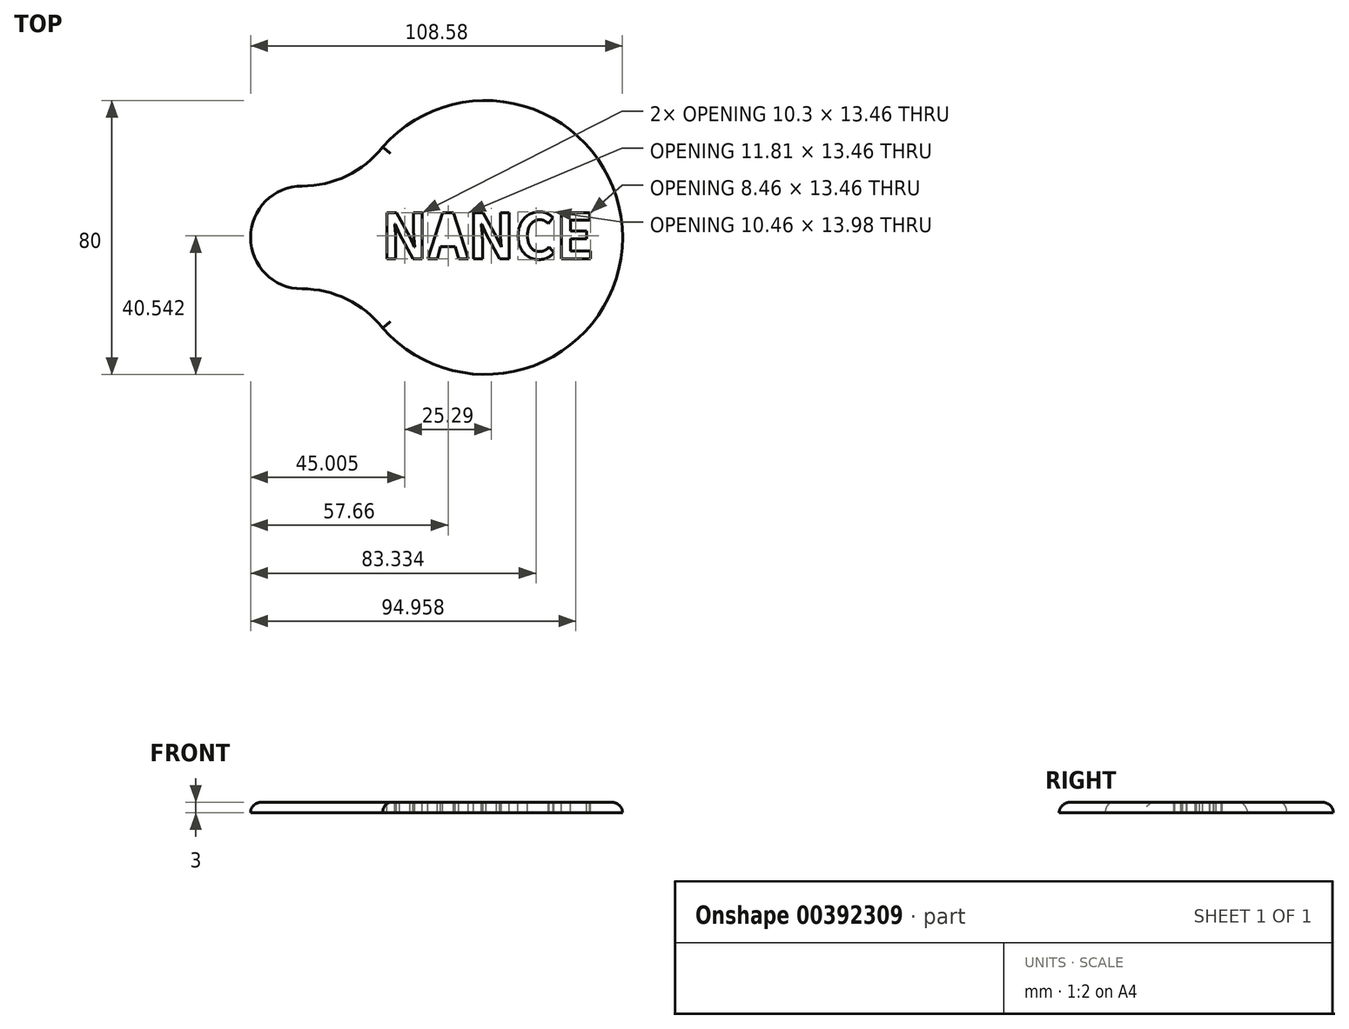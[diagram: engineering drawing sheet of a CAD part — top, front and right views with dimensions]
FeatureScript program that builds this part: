
annotation { "Feature Type Name" : "Feature", "Feature Type Description" : "" }
export const myFeature = defineFeature(function(context is Context, id is Id, definition is map)
    precondition{}
    {
        {
            var Q0;
            Q0=qCreatedBy(makeId("Top.planeOp"),FACE);
            var sketch = newSketch(context, id + "F0", { "sketchPlane" : qUnion([Q0])});
            skLineSegment(sketch, "E0.left", {"start": v(30, 0) * mm, "end": v(30, 0) * mm});
            skLineSegment(sketch, "E0.right", {"start": v(-30, -10) * mm, "end": v(-30, -10) * mm});
            skPoint(sketch, "E0.middle", {"position": v(0, 0) * mm});
            skPoint(sketch, "E1.visualSharp", {"position": v(30, 40) * mm});
            skPoint(sketch, "E2.visualSharp", {"position": v(30, -40) * mm});
            skPoint(sketch, "E3.visualSharp", {"position": v(-30, -40) * mm});
            skLineSegment(sketch, "E4.bottom", {"start": v(-45, 15) * mm, "end": v(-45, 15) * mm});
            skLineSegment(sketch, "E4.top", {"start": v(-45, -15) * mm, "end": v(-45, -15) * mm});
            skPoint(sketch, "E4.middle", {"position": v(-37.5, 0) * mm});
            skArc(sketch, "E5", {"start": v(-45, -15) * mm, "mid": v(-60, 0) * mm, "end": v(-45, 15) * mm});
            skPoint(sketch, "E6.visualSharp", {"position": v(-30, 40) * mm});
            skPoint(sketch, "E7.newPointA", {"position": v(-30, 15) * mm});
            skArc(sketch, "E7.filletArc", {"start": v(-45, 15) * mm, "mid": v(-31.9, 18.01) * mm, "end": v(-21.43, 26.44) * mm});
            skPoint(sketch, "E8.newPointA", {"position": v(-30, -15) * mm});
            skArc(sketch, "E8.filletArc", {"start": v(-21.43, -26.44) * mm, "mid": v(-31.9, -18.01) * mm, "end": v(-45, -15) * mm});
            skArc(sketch, "E9", {"start": v(-21.43, -26.44) * mm, "mid": v(48.58, 0) * mm, "end": v(-21.43, 26.44) * mm});
            skSolve(sketch);
        }
        {
            var Q0;
            Q0=qSketchRegion(id+"F0",true);
            extrude(context, id + "F1", {"entities" : qUnion([Q0]), "depth" : 3 * mm});
        }
        {
            var Q0;
            Q0=makeQuery(id+"F1.opExtrude","CAP_EDGE",EDGE,{"disambiguationData":[OSD([sQuery(id+"F0.wireOp",EDGE,"E9")])],"isStart":false});
            var Q1;
            Q1=makeQuery(id+"F1.opExtrude","CAP_EDGE",EDGE,{"disambiguationData":[OSD([sQuery(id+"F0.wireOp",EDGE,"E7.filletArc")])],"isStart":false});
            var Q2;
            Q2=makeQuery(id+"F1.opExtrude","CAP_EDGE",EDGE,{"disambiguationData":[OSD([sQuery(id+"F0.wireOp",EDGE,"E5")])],"isStart":false});
            fillet(context, id + "F2", {"entities" : qUnion([Q0, Q1, Q2]), "radius" : 3 * mm, "tangentPropagation" : true, "allowEdgeOverflow" : false});
        }
        {
            var Q0;
            Q0=makeQuery(id+"F1.opExtrude","CAP_FACE",FACE,{"disambiguationData":[OSD([sQuery(id+"F0.wireOp",EDGE,"E5"),sQuery(id+"F0.wireOp",EDGE,"E7.filletArc"),sQuery(id+"F0.wireOp",EDGE,"E8.filletArc"),sQuery(id+"F0.wireOp",EDGE,"E9")])],"isStart":false});
            var sketch = newSketch(context, id + "F3", { "sketchPlane" : qUnion([Q0])});
            skText(sketch, "E10", { "text": "NANCE\n", "fontName": "NotoSansCJKsc-Bold.otf"});
            const initialGuessF3  = {"E10": [-0.0218, -0.00619, 1, 0, 0.0131]};
            skSetInitialGuess(sketch, initialGuessF3);
            skSolve(sketch);
        }
        {
            var Q0;
            Q0 = qSketchRegion(id + "F3", true);
            extrude(context, id + "F4", {"entities" : qUnion([Q0]), "operationType" : NewBodyOperationType.REMOVE, "oppositeDirection" : true, "depth" : 25 * mm});
        }
        {
            var Q0;
            Q0=makeQuery(id+"F4.boolean.opBoolean","SPLIT",FACE,{"disambiguationData":[TD([makeQuery(id+"F4.opExtrude","SWEPT_FACE",FACE,{"disambiguationData":[OSD([sQuery(id+"F3.wireOp",EDGE,"E10.sketch_text.stroke-16")])]})])],"derivedFrom":makeQuery(id+"F1.opExtrude","CAP_FACE",FACE,{"disambiguationData":[OSD([sQuery(id+"F0.wireOp",EDGE,"E5"),sQuery(id+"F0.wireOp",EDGE,"E7.filletArc"),sQuery(id+"F0.wireOp",EDGE,"E8.filletArc"),sQuery(id+"F0.wireOp",EDGE,"E9")])],"isStart":false})});
            var sketch = newSketch(context, id + "F5", { "sketchPlane" : qUnion([Q0])});
            skLineSegment(sketch, "E11", {"start": v(-2.48, 7.06) * mm, "end": v(1.2, -1.87) * mm});
            skLineSegment(sketch, "E12", {"start": v(1.2, -1.87) * mm, "end": v(-4.83, -1.62) * mm});
            skLineSegment(sketch, "E13", {"start": v(-4.83, -1.62) * mm, "end": v(-2.48, 7.06) * mm});
            skSolve(sketch);
        }
        {
            var Q0;
            Q0 = qSketchRegion(id + "F5", true);
            extrude(context, id + "F6", {"entities" : qUnion([Q0]), "operationType" : NewBodyOperationType.REMOVE, "oppositeDirection" : true, "depth" : 25 * mm});
        }
    });
